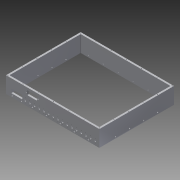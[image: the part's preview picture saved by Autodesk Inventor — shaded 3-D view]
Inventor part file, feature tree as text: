
AUTODESK INVENTOR PART (.ipt)
format: ipt  version: 2016 (Build 200138000, 138)  size: 473,088 bytes
history: native  units: in
note: dims shown in document units (in); Inventor stores cm internally (conversion verified against a paired STEP export)
features: hole x14, pattern_linear x10, other x9, fillet x8, extrude x3
ambient origin geometry x8: Origin, YZ Plane, XZ Plane, XY Plane, X Axis, Y Axis, Z Axis, Center Point
bodies: Solid1 (feature_tree)
feature tree (44):
  extrude  "Extrusion1"  Depth=9.626in
  other  "left-2"
  other  "left-1"
  other  "bottom-1"
  hole  "Hole8"  [1 undecoded]
  hole  "Hole9"  [1 undecoded]
  other  "front-1"
  hole  "Hole10"  [1 undecoded]
  other  "right-1"
  hole  "Hole11"  [1 undecoded]
  hole  "Hole12"  [1 undecoded]
  pattern_linear  "Rectangular Pattern9"  Spacing1=1.75in  [1 undecoded]
  pattern_linear  "Rectangular Pattern10"  Spacing1=0.0935in  [1 undecoded]
  pattern_linear  "Rectangular Pattern11"  Spacing1=0.0935in  [1 undecoded]
  pattern_linear  "Rectangular Pattern12"  Count1=6 Spacing1=1.562in
  hole  "Hole13"  [1 undecoded]
  hole  "Hole16"  [1 undecoded]
  hole  "Hole17"  [1 undecoded]
  extrude  "Extrusion2"  Depth=2.3622in
  hole  "Hole18"  [1 undecoded]
  hole  "Hole19"  [1 undecoded]
  hole  "Hole20"  [1 undecoded]
  hole  "Hole21"  [1 undecoded]
  pattern_linear  "Rectangular Pattern13"  Spacing1=0.48in  [1 undecoded]
  hole  "Hole22"  [1 undecoded]
  pattern_linear  "Rectangular Pattern14"  Spacing1=0.4094in  [1 undecoded]
  pattern_linear  "Rectangular Pattern15"  Spacing1=2.05in  [1 undecoded]
  pattern_linear  "Rectangular Pattern16"  Spacing1=0.41in  [1 undecoded]
  pattern_linear  "Rectangular Pattern17"  Spacing1=0.368in  [1 undecoded]
  pattern_linear  "Rectangular Pattern19"  Spacing1=1.0in  [1 undecoded]
  fillet  "Fillet1"  Radius=1.75in
  fillet  "Fillet2"  Radius=0.185in
  fillet  "Fillet3"  Radius=1.0in
  fillet  "Fillet4"  Radius=0.185in
  fillet  "Fillet5"  Radius=0.185in
  fillet  "Fillet6"  Radius=1.75in
  fillet  "Fillet7"  Radius=0.185in
  fillet  "Fillet8"  Radius=0.3937in
  other  "front-2"
  hole  "Hole23"  [1 undecoded]
  extrude  "Extrusion5"  Depth=2.05in
  other  "Ext-Sketch"
  other  "back-1"
  other  "top"
note: 23 required parameter values undecoded (feature->parameter linkage not recoverable at this tier; creation-order binding heuristic only, values carry confidence <= 0.55)
